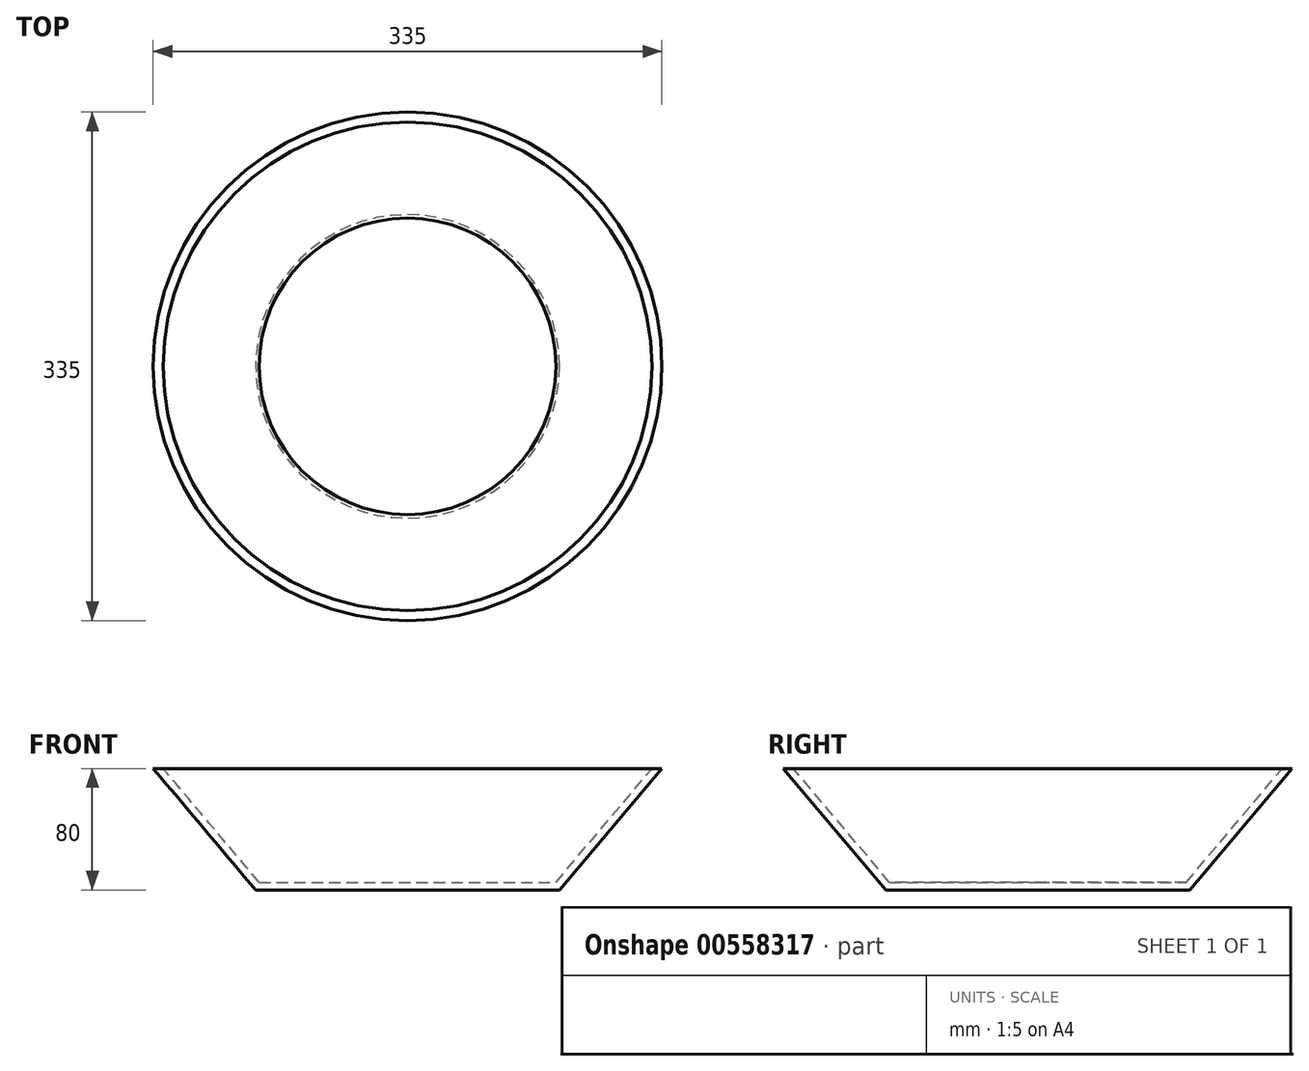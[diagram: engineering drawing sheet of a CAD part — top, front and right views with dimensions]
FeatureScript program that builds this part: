
annotation { "Feature Type Name" : "Feature", "Feature Type Description" : "" }
export const myFeature = defineFeature(function(context is Context, id is Id, definition is map)
    precondition{}
    {
        {
            var Q0;
            Q0=qCreatedBy(makeId("Front.planeOp"),FACE);
            var sketch = newSketch(context, id + "F0", { "sketchPlane" : qUnion([Q0])});
            skLineSegment(sketch, "E0", {"start": v(0, 0) * mm, "end": v(0, 236.55) * mm, "construction": true});
            skLineSegment(sketch, "E1", {"start": v(0, 0) * mm, "end": v(100, 0) * mm});
            skLineSegment(sketch, "E2", {"start": v(100, 0) * mm, "end": v(167.5, 80) * mm});
            skLineSegment(sketch, "E3", {"start": v(167.5, 80) * mm, "end": v(160.96, 80) * mm});
            skLineSegment(sketch, "E4", {"start": v(160.96, 80) * mm, "end": v(97.68, 5) * mm});
            skLineSegment(sketch, "E5", {"start": v(97.68, 5) * mm, "end": v(0, 5) * mm});
            skLineSegment(sketch, "E6", {"start": v(0, 5) * mm, "end": v(0, 0) * mm});
            skSolve(sketch);
        }
        {
            var Q0;
            Q0 = qSketchRegion(id + "F0", true);
            var Q1;
            Q1=sQuery(id+"F0.wireOp",EDGE,"E0");
            revolve(context, id + "F1", {"entities" : qUnion([Q0]), "axis" : qUnion([Q1]), "revolveType" : RevolveType.FULL});
        }
    });
